FCSTD DOCUMENT  (FreeCAD 0.18R)
Label: PrusaMini-BracketV2
License: CreativeCommons Attribution
LicenseURL: http://creativecommons.org/licenses/by/4.0/
objects: Sketcher::SketchObject×1, PartDesign::Body×1
note: 2 computed .brp shape members not serialized (recipe doc carries the construction recipe); baked Part::Feature solids carry a one-line shape summary decoded from their .brp

FEATURE [Sketcher::SketchObject] Sketch
  MapMode = 5
  Placement = pos=(0,0,0) rot=(1,0,0;1.5708rad)
  Support = -> [XZ_Plane]
  sketch-geometry (12):
    g0: LineSegment StartX=-29.107 StartY=0 StartZ=0 EndX=-29.107 EndY=2 EndZ=0
    g1: LineSegment StartX=-29.107 StartY=2 StartZ=0 EndX=0.89303 EndY=2 EndZ=0
    g2: LineSegment StartX=0.89303 StartY=2 StartZ=0 EndX=0.89303 EndY=3.421 EndZ=0
    g3: LineSegment StartX=0.89303 StartY=3.421 StartZ=0 EndX=-2.92267 EndY=3.90587 EndZ=0
    g4: LineSegment StartX=-2.92267 StartY=3.90587 StartZ=0 EndX=-2.92267 EndY=4.74092 EndZ=0
    g5: LineSegment StartX=-2.92267 StartY=4.74092 StartZ=0 EndX=0.964433 EndY=4.74092 EndZ=0
    g6: LineSegment StartX=-29.107 StartY=0 StartZ=0 EndX=22.1557 EndY=0 EndZ=0
    g7: LineSegment StartX=2.72594 StartY=2.3974 StartZ=0 EndX=2.72594 EndY=10.3708 EndZ=0
    g8: ArcOfCircle CenterX=1.84519 CenterY=10.3708 CenterZ=0 NormalX=0 NormalY=0 NormalZ=1 AngleXU=0 Radius=0.880753 StartAngle=1e-15 EndAngle=3.14159
    g9: LineSegment StartX=0.964433 StartY=10.3708 StartZ=0 EndX=0.964433 EndY=4.74092 EndZ=0
    g10: LineSegment StartX=2.72594 StartY=2.3974 StartZ=0 EndX=22.1557 EndY=2.3974 EndZ=0
    g11: LineSegment StartX=22.1557 StartY=2.3974 StartZ=0 EndX=22.1557 EndY=0 EndZ=0
  constraints (25):
    c: Coincident(g0,g1)
    c: Coincident(g1,g2)
    c: Coincident(g2,g3)
    c: Coincident(g3,g4)
    c: Coincident(g4,g5)
    c: Tangent(g7,g8) = -1.5708
    c: Tangent(g8,g9) = -1.5708
    c: Coincident(g5,g9)
    c: Coincident(g0,g6)
    c: Vertical(g0)
    c: Horizontal(g1)
    c: Horizontal(g6)
    c: Vertical(g2)
    c: Vertical(g7)
    c: Vertical(g9)
    c: Horizontal(g5)
    c: Vertical(g4)
    c: Coincident(g10,g11)
    c: Coincident(g6,g11)
    c: Vertical(g11)
    c: Horizontal(g10)
    c: Coincident(g7,g10)
    c: DistanceX(g1,g1) = 30
    c: PointOnObject(g0,g-1)
    c: DistanceY(g0,g0) = 2
FEATURE [PartDesign::Body] Body
  Group = -> [Sketch]
  Origin = -> Origin
